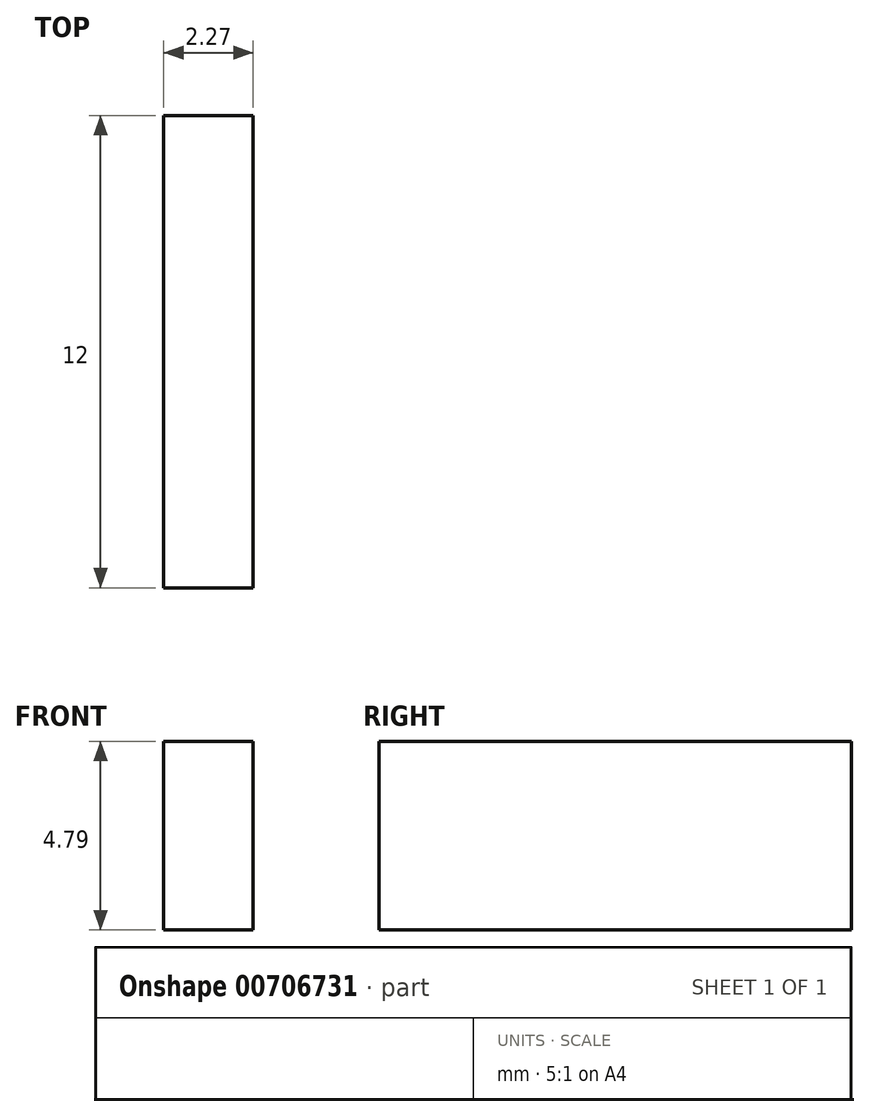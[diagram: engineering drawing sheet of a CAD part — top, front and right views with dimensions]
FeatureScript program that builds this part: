
annotation { "Feature Type Name" : "Feature", "Feature Type Description" : "" }
export const myFeature = defineFeature(function(context is Context, id is Id, definition is map)
    precondition{}
    {
        {
            var Q0;
            Q0=qCreatedBy(makeId("Front.planeOp"),FACE);
            var sketch = newSketch(context, id + "F0", { "sketchPlane" : qUnion([Q0])});
            skLineSegment(sketch, "E0.bottom", {"start": v(1.3, 9.65) * mm, "end": v(-0.97, 9.65) * mm});
            skLineSegment(sketch, "E0.top", {"start": v(1.3, 4.86) * mm, "end": v(-0.97, 4.86) * mm});
            skLineSegment(sketch, "E0.left", {"start": v(1.3, 9.65) * mm, "end": v(1.3, 4.86) * mm});
            skLineSegment(sketch, "E0.right", {"start": v(-0.97, 9.65) * mm, "end": v(-0.97, 4.86) * mm});
            skSolve(sketch);
        }
        {
            var Q0;
            Q0=makeQuery(id+"F0.imprint","IMPRINT",FACE,{"disambiguationData":[TD([[makeQuery(id+"F0.imprint","IMPRINT",EDGE,{"derivedFrom":sQuery(id+"F0.wireOp",EDGE,"E0.bottom")}),1.0]])]});
            extrude(context, id + "F1", {"entities" : qUnion([Q0]), "depth" : 12 * mm, "offsetDistance" : 25 * mm});
        }
    });
